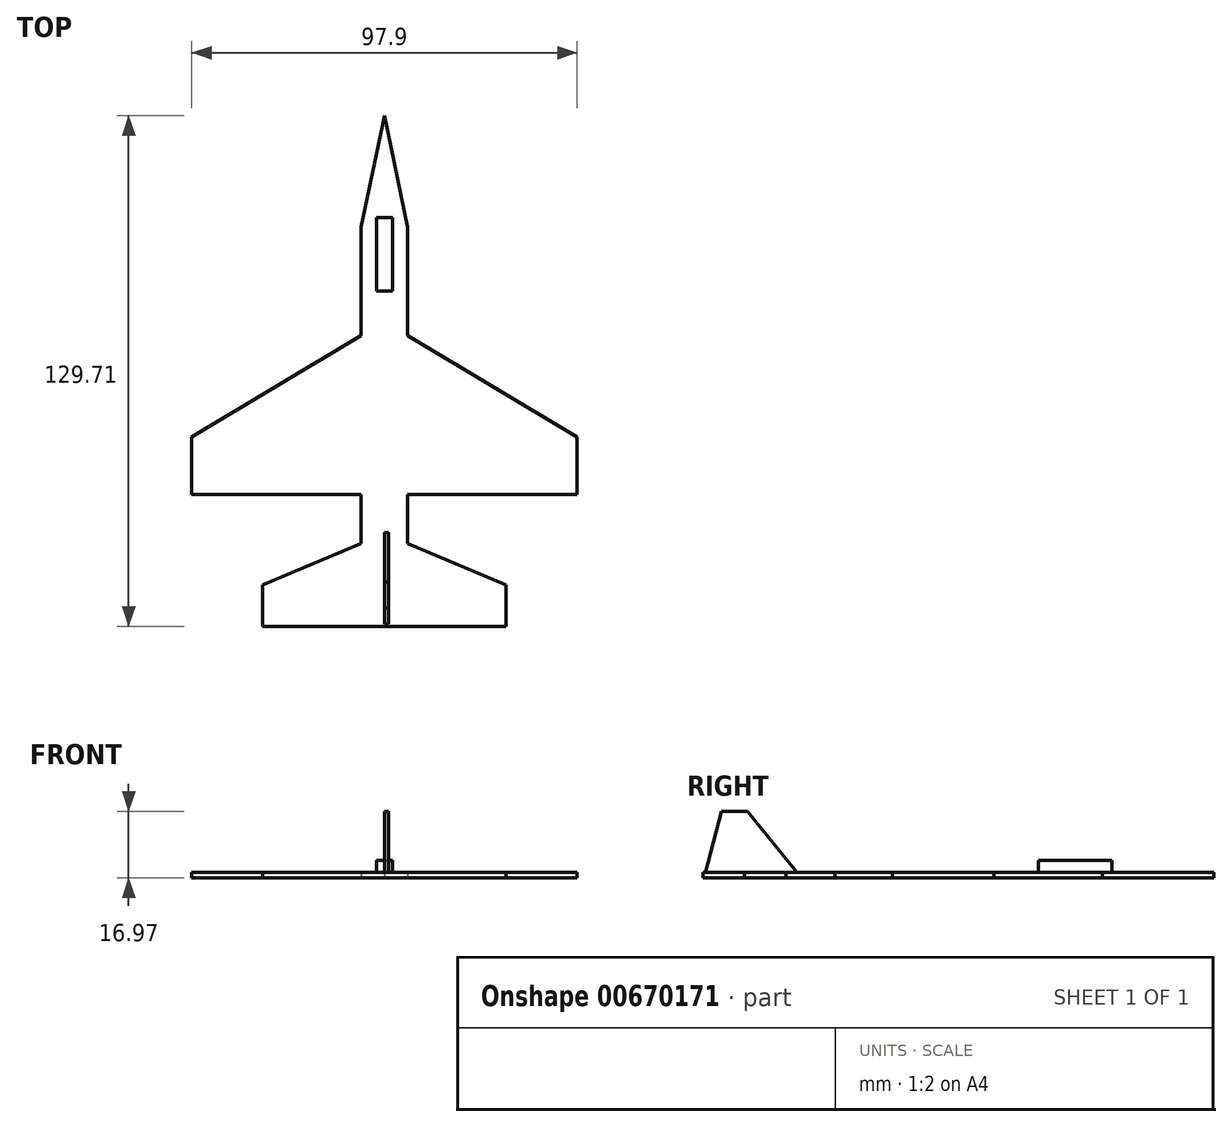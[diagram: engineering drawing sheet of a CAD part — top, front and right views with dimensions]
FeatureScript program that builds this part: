
annotation { "Feature Type Name" : "Feature", "Feature Type Description" : "" }
export const myFeature = defineFeature(function(context is Context, id is Id, definition is map)
    precondition{}
    {
        {
            var Q0;
            Q0=qCreatedBy(makeId("Top.planeOp"),FACE);
            var sketch = newSketch(context, id + "F0", { "sketchPlane" : qUnion([Q0])});
            skLineSegment(sketch, "E0", {"start": v(0, 55.84) * mm, "end": v(-5.88, 27.54) * mm});
            skLineSegment(sketch, "E1", {"start": v(-5.88, 27.54) * mm, "end": v(-5.88, 0) * mm});
            skLineSegment(sketch, "E2", {"start": v(-5.88, 0) * mm, "end": v(-48.95, -25.8) * mm});
            skLineSegment(sketch, "E3", {"start": v(-48.95, -25.8) * mm, "end": v(-48.95, -40.31) * mm});
            skLineSegment(sketch, "E4", {"start": v(-48.95, -40.31) * mm, "end": v(-5.88, -40.31) * mm});
            skLineSegment(sketch, "E5", {"start": v(-5.88, -40.31) * mm, "end": v(-5.88, -52.83) * mm});
            skLineSegment(sketch, "E6", {"start": v(-5.88, -52.83) * mm, "end": v(-30.92, -63.35) * mm});
            skLineSegment(sketch, "E7", {"start": v(-30.92, -63.35) * mm, "end": v(-30.92, -73.87) * mm});
            skLineSegment(sketch, "E8", {"start": v(-30.92, -73.87) * mm, "end": v(0, -73.87) * mm});
            skLineSegment(sketch, "E9", {"start": v(0, -73.87) * mm, "end": v(0, 55.84) * mm, "construction": true});
            skLineSegment(sketch, "E10.MirrorCS", {"start": v(5.88, -40.31) * mm, "end": v(5.88, -52.83) * mm});
            skLineSegment(sketch, "E11.MirrorCS", {"start": v(5.88, 0) * mm, "end": v(48.95, -25.8) * mm});
            skLineSegment(sketch, "E12.MirrorCS", {"start": v(48.95, -40.31) * mm, "end": v(5.88, -40.31) * mm});
            skLineSegment(sketch, "E13.MirrorCS", {"start": v(5.88, -52.83) * mm, "end": v(30.92, -63.35) * mm});
            skLineSegment(sketch, "E14.MirrorCS", {"start": v(48.95, -25.8) * mm, "end": v(48.95, -40.31) * mm});
            skLineSegment(sketch, "E15.MirrorCS", {"start": v(30.92, -63.35) * mm, "end": v(30.92, -73.87) * mm});
            skLineSegment(sketch, "E16.MirrorCS", {"start": v(5.88, 27.54) * mm, "end": v(5.88, 0) * mm});
            skLineSegment(sketch, "E17.MirrorCS", {"start": v(30.92, -73.87) * mm, "end": v(0, -73.87) * mm});
            skLineSegment(sketch, "E18", {"start": v(0, 55.84) * mm, "end": v(5.88, 27.54) * mm});
            skSolve(sketch);
        }
        {
            var Q0;
            Q0=makeQuery(id+"F0.imprint","IMPRINT",FACE,{"disambiguationData":[TD([[makeQuery(id+"F0.imprint","IMPRINT",EDGE,{"derivedFrom":sQuery(id+"F0.wireOp",EDGE,"E0")}),1.0]])]});
            extrude(context, id + "F1", {"entities" : qUnion([Q0]), "depth" : 1.5 * mm, "offsetDistance" : 25 * mm});
        }
        {
            var Q0;
            Q0=makeQuery(id+"F1.opExtrude","CAP_FACE",FACE,{"disambiguationData":[OSD([sQuery(id+"F0.wireOp",EDGE,"E0"),sQuery(id+"F0.wireOp",EDGE,"E1"),sQuery(id+"F0.wireOp",EDGE,"E2"),sQuery(id+"F0.wireOp",EDGE,"E3"),sQuery(id+"F0.wireOp",EDGE,"E4"),sQuery(id+"F0.wireOp",EDGE,"E5"),sQuery(id+"F0.wireOp",EDGE,"E6"),sQuery(id+"F0.wireOp",EDGE,"E7"),sQuery(id+"F0.wireOp",EDGE,"E8"),sQuery(id+"F0.wireOp",EDGE,"E10.MirrorCS"),sQuery(id+"F0.wireOp",EDGE,"E11.MirrorCS"),sQuery(id+"F0.wireOp",EDGE,"E12.MirrorCS"),sQuery(id+"F0.wireOp",EDGE,"E13.MirrorCS"),sQuery(id+"F0.wireOp",EDGE,"E14.MirrorCS"),sQuery(id+"F0.wireOp",EDGE,"E15.MirrorCS"),sQuery(id+"F0.wireOp",EDGE,"E16.MirrorCS"),sQuery(id+"F0.wireOp",EDGE,"E17.MirrorCS"),sQuery(id+"F0.wireOp",EDGE,"E18")])],"isStart":false});
            var sketch = newSketch(context, id + "F2", { "sketchPlane" : qUnion([Q0])});
            skLineSegment(sketch, "E19.bottom", {"start": v(-2.04, 30) * mm, "end": v(0, 30) * mm});
            skLineSegment(sketch, "E19.top", {"start": v(-2.04, 11.27) * mm, "end": v(0, 11.27) * mm});
            skLineSegment(sketch, "E19.left", {"start": v(0, 30) * mm, "end": v(0, 11.27) * mm});
            skLineSegment(sketch, "E19.right", {"start": v(-2.04, 30) * mm, "end": v(-2.04, 11.27) * mm});
            skLineSegment(sketch, "E20.MirrorCS", {"start": v(2.04, 30) * mm, "end": v(2.04, 11.27) * mm});
            skLineSegment(sketch, "E21.MirrorCS", {"start": v(2.04, 11.27) * mm, "end": v(0, 11.27) * mm});
            skLineSegment(sketch, "E22.MirrorCS", {"start": v(2.04, 30) * mm, "end": v(0, 30) * mm});
            skSolve(sketch);
        }
        {
            var Q0;
            Q0 = qSketchRegion(id + "F2", true);
            var Q1;
            Q1 = qSketchRegion(id + "F6", true);
            extrude(context, id + "F3", {"entities" : qUnion([Q0, Q1]), "operationType" : NewBodyOperationType.ADD, "depth" : 3 * mm, "offsetDistance" : 25 * mm});
        }
        {
            var Q0;
            Q0=qCreatedBy(makeId("Right.planeOp"),FACE);
            var sketch = newSketch(context, id + "F4", { "sketchPlane" : qUnion([Q0])});
            skLineSegment(sketch, "E23", {"start": v(-73.73, 0) * mm, "end": v(-69.17, 16.97) * mm});
            skLineSegment(sketch, "E24", {"start": v(-69.17, 16.97) * mm, "end": v(-62.6, 16.97) * mm});
            skLineSegment(sketch, "E25", {"start": v(-62.6, 16.97) * mm, "end": v(-48.74, 0) * mm});
            skLineSegment(sketch, "E26", {"start": v(-48.74, 0) * mm, "end": v(-73.73, 0) * mm});
            skSolve(sketch);
        }
        {
            var Q0;
            Q0 = qSketchRegion(id + "F4", true);
            extrude(context, id + "F5", {"entities" : qUnion([Q0]), "operationType" : NewBodyOperationType.ADD, "depth" : 1 * mm, "offsetDistance" : 25 * mm});
        }
    });
